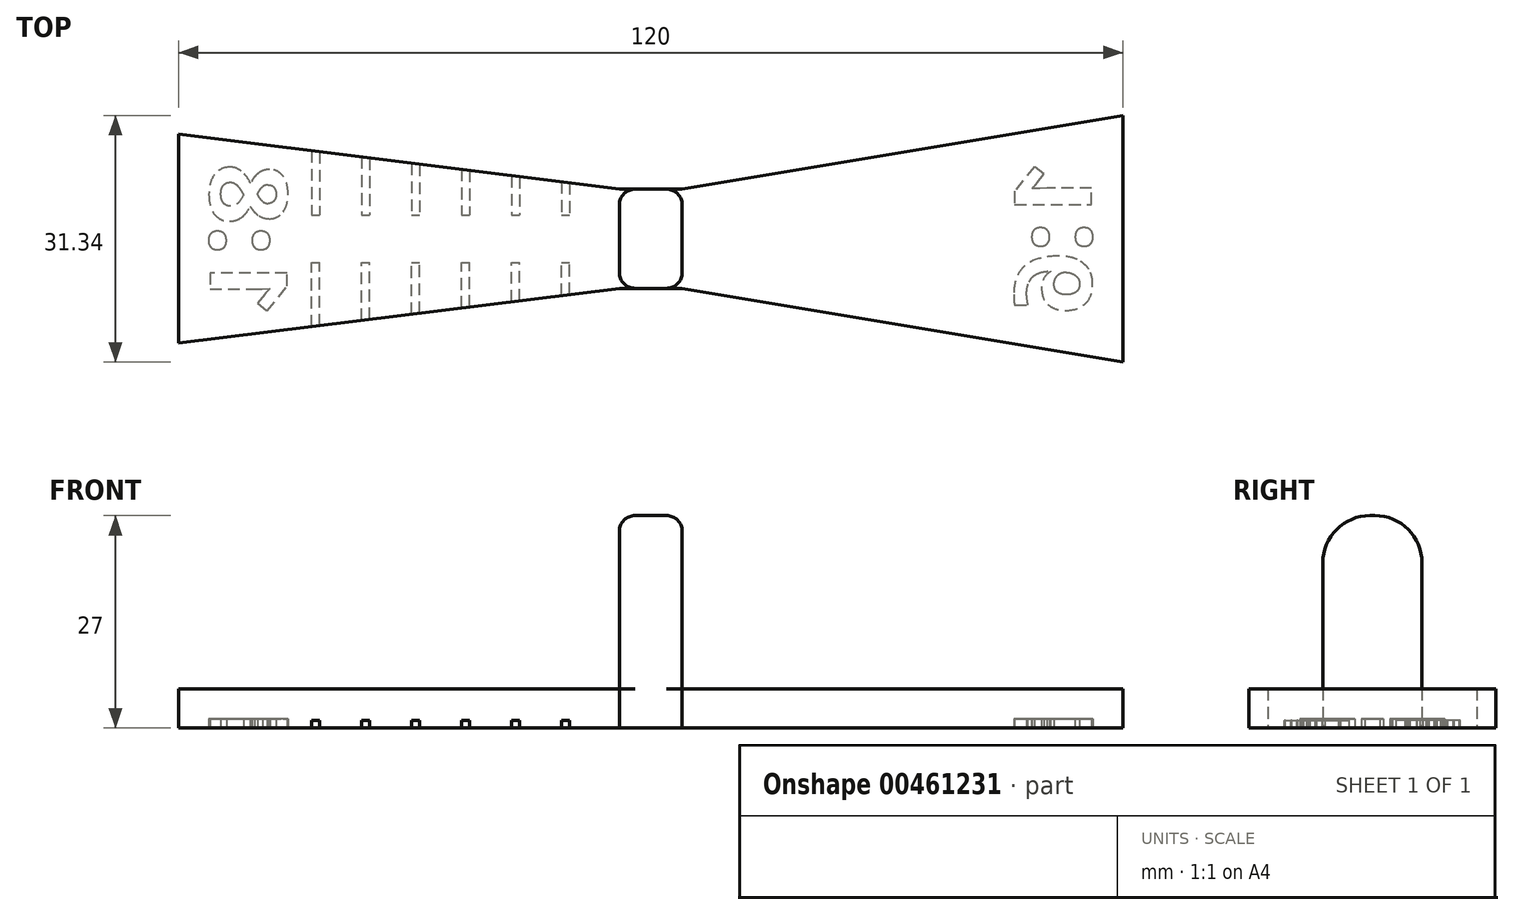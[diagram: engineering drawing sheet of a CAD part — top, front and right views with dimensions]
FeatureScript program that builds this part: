
annotation { "Feature Type Name" : "Feature", "Feature Type Description" : "" }
export const myFeature = defineFeature(function(context is Context, id is Id, definition is map)
    precondition{}
    {
        {
            var Q0;
            Q0=qCreatedBy(makeId("Top.planeOp"),FACE);
            var sketch = newSketch(context, id + "F0", { "sketchPlane" : qUnion([Q0])});
            skLineSegment(sketch, "E0", {"start": v(-4, 6.3) * mm, "end": v(-60, 13.28) * mm});
            skLineSegment(sketch, "E1", {"start": v(-60, 13.28) * mm, "end": v(-60, -13.28) * mm});
            skLineSegment(sketch, "E2", {"start": v(-60, -13.28) * mm, "end": v(-4, -6.3) * mm});
            skLineSegment(sketch, "E3", {"start": v(-4, -6.3) * mm, "end": v(4, -6.3) * mm});
            skLineSegment(sketch, "E4", {"start": v(4, -6.3) * mm, "end": v(60, -15.67) * mm});
            skLineSegment(sketch, "E5", {"start": v(60, -15.67) * mm, "end": v(60, 15.67) * mm});
            skLineSegment(sketch, "E6", {"start": v(60, 15.67) * mm, "end": v(4, 6.3) * mm});
            skLineSegment(sketch, "E7", {"start": v(4, 6.3) * mm, "end": v(-4, 6.3) * mm});
            skSolve(sketch);
        }
        {
            var Q0;
            Q0=makeQuery(id+"F0.imprint","IMPRINT",FACE,{"disambiguationData":[TD([[makeQuery(id+"F0.imprint","IMPRINT",EDGE,{"derivedFrom":sQuery(id+"F0.wireOp",EDGE,"E0")}),1.0]])]});
            extrude(context, id + "F1", {"entities" : qUnion([Q0]), "depth" : 5 * mm});
        }
        {
            var Q0;
            Q0=makeQuery(id+"F1.opExtrude","CAP_FACE",FACE,{"disambiguationData":[OSD([sQuery(id+"F0.wireOp",EDGE,"E0"),sQuery(id+"F0.wireOp",EDGE,"E1"),sQuery(id+"F0.wireOp",EDGE,"E2"),sQuery(id+"F0.wireOp",EDGE,"E3"),sQuery(id+"F0.wireOp",EDGE,"E4"),sQuery(id+"F0.wireOp",EDGE,"E5"),sQuery(id+"F0.wireOp",EDGE,"E6"),sQuery(id+"F0.wireOp",EDGE,"E7")])],"isStart":false});
            var sketch = newSketch(context, id + "F2", { "sketchPlane" : qUnion([Q0])});
            skLineSegment(sketch, "E8", {"start": v(-4, 6.3) * mm, "end": v(-4, -6.3) * mm});
            skLineSegment(sketch, "E9", {"start": v(-4, -6.3) * mm, "end": v(4, -6.3) * mm});
            skLineSegment(sketch, "E10", {"start": v(4, -6.3) * mm, "end": v(4, 6.3) * mm});
            skLineSegment(sketch, "E11", {"start": v(4, 6.3) * mm, "end": v(-4, 6.3) * mm});
            skSolve(sketch);
        }
        {
            var Q0;
            Q0 = qSketchRegion(id + "F2", true);
            extrude(context, id + "F3", {"entities" : qUnion([Q0]), "operationType" : NewBodyOperationType.ADD, "depth" : 22 * mm});
        }
        {
            var Q0;
            Q0=makeQuery(id+"F3.opExtrude","CAP_EDGE",EDGE,{"disambiguationData":[OSD([sQuery(id+"F2.wireOp",EDGE,"E9")])],"isStart":false});
            var Q1;
            Q1=makeQuery(id+"F3.opExtrude","CAP_EDGE",EDGE,{"disambiguationData":[OSD([sQuery(id+"F2.wireOp",EDGE,"E11")])],"isStart":false});
            fillet(context, id + "F4", {"entities" : qUnion([Q0, Q1]), "radius" : 6 * mm, "tangentPropagation" : true, "allowEdgeOverflow" : false});
        }
        {
            var Q0;
            Q0=makeQuery(id+"F3.opExtrude","CAP_EDGE",EDGE,{"disambiguationData":[OSD([sQuery(id+"F2.wireOp",EDGE,"E8")])],"isStart":false});
            var Q1;
            Q1=makeQuery(id+"F3.opExtrude","CAP_EDGE",EDGE,{"disambiguationData":[OSD([sQuery(id+"F2.wireOp",EDGE,"E10")])],"isStart":false});
            fillet(context, id + "F5", {"entities" : qUnion([Q0, Q1]), "radius" : 2 * mm, "tangentPropagation" : true, "allowEdgeOverflow" : false});
        }
        {
            var Q0;
            Q0=makeQuery(id+"F1.opExtrude","CAP_FACE",FACE,{"disambiguationData":[OSD([sQuery(id+"F0.wireOp",EDGE,"E0"),sQuery(id+"F0.wireOp",EDGE,"E1"),sQuery(id+"F0.wireOp",EDGE,"E2"),sQuery(id+"F0.wireOp",EDGE,"E3"),sQuery(id+"F0.wireOp",EDGE,"E4"),sQuery(id+"F0.wireOp",EDGE,"E5"),sQuery(id+"F0.wireOp",EDGE,"E6"),sQuery(id+"F0.wireOp",EDGE,"E7")])],"isStart":true});
            var sketch = newSketch(context, id + "F6", { "sketchPlane" : qUnion([Q0])});
            skText(sketch, "E12", { "text": "1:8", "fontName": "OpenSans-Bold.ttf"});
            skText(sketch, "E13", { "text": "1:6", "fontName": "OpenSans-Bold.ttf"});
            const initialGuessF6  = {"E12": [-0.056, 0.01, 0, -1, 0.00988], "E13": [0.056, -0.01, 0, 1, 0.00986]};
            skSetInitialGuess(sketch, initialGuessF6);
            skSolve(sketch);
        }
        {
            var Q0;
            Q0 = qSketchRegion(id + "F6", true);
            extrude(context, id + "F7", {"entities" : qUnion([Q0]), "operationType" : NewBodyOperationType.REMOVE, "oppositeDirection" : true, "depth" : 1.2 * mm});
        }
        {
            var Q0;
            {var subQ0=sQuery(id+"F0.wireOp",EDGE,"E7");var subQ1=sQuery(id+"F0.wireOp",EDGE,"E0");var subQ2=sQuery(id+"F0.wireOp",EDGE,"E6");var subQ3=sQuery(id+"F0.wireOp",EDGE,"E5");var subQ4=sQuery(id+"F0.wireOp",EDGE,"E4");var subQ5=sQuery(id+"F0.wireOp",EDGE,"E1");var subQ6=sQuery(id+"F0.wireOp",EDGE,"E2");var subQ7=sQuery(id+"F0.wireOp",EDGE,"E3");Q0=makeQuery(id+"F7.boolean.opBoolean","SPLIT",FACE,{"disambiguationData":[TD([makeQuery(id+"F1.opExtrude","SWEPT_FACE",FACE,{"disambiguationData":[OSD([subQ1])]})])],"derivedFrom":makeQuery(id+"F1.opExtrude","CAP_FACE",FACE,{"disambiguationData":[OSD([subQ1,subQ5,subQ6,subQ7,subQ4,subQ3,subQ2,subQ0])],"isStart":true})});}
            var sketch = newSketch(context, id + "F8", { "sketchPlane" : qUnion([Q0])});
            skLineSegment(sketch, "E14.bottom", {"start": v(-11.35, 13) * mm, "end": v(-10.35, 13) * mm});
            skLineSegment(sketch, "E14.top", {"start": v(-11.35, 3) * mm, "end": v(-10.35, 3) * mm});
            skLineSegment(sketch, "E14.left", {"start": v(-11.35, 13) * mm, "end": v(-11.35, 3) * mm});
            skLineSegment(sketch, "E14.right", {"start": v(-10.35, 13) * mm, "end": v(-10.35, 3) * mm});
            skLineSegment(sketch, "E15.1.0.0", {"start": v(-16.7, 13) * mm, "end": v(-16.7, 3) * mm});
            skLineSegment(sketch, "E15.1.0.1", {"start": v(-17.7, 13) * mm, "end": v(-16.7, 13) * mm});
            skLineSegment(sketch, "E15.1.0.2", {"start": v(-17.7, 13) * mm, "end": v(-17.7, 3) * mm});
            skLineSegment(sketch, "E15.1.0.3", {"start": v(-17.7, 3) * mm, "end": v(-16.7, 3) * mm});
            skLineSegment(sketch, "E15.2.0.0", {"start": v(-23.05, 13) * mm, "end": v(-23.05, 3) * mm});
            skLineSegment(sketch, "E15.2.0.1", {"start": v(-24.05, 13) * mm, "end": v(-23.05, 13) * mm});
            skLineSegment(sketch, "E15.2.0.2", {"start": v(-24.05, 13) * mm, "end": v(-24.05, 3) * mm});
            skLineSegment(sketch, "E15.2.0.3", {"start": v(-24.05, 3) * mm, "end": v(-23.05, 3) * mm});
            skLineSegment(sketch, "E15.3.0.0", {"start": v(-29.4, 13) * mm, "end": v(-29.4, 3) * mm});
            skLineSegment(sketch, "E15.3.0.1", {"start": v(-30.4, 13) * mm, "end": v(-29.4, 13) * mm});
            skLineSegment(sketch, "E15.3.0.2", {"start": v(-30.4, 13) * mm, "end": v(-30.4, 3) * mm});
            skLineSegment(sketch, "E15.3.0.3", {"start": v(-30.4, 3) * mm, "end": v(-29.4, 3) * mm});
            skLineSegment(sketch, "E15.4.0.0", {"start": v(-35.75, 13) * mm, "end": v(-35.75, 3) * mm});
            skLineSegment(sketch, "E15.4.0.1", {"start": v(-36.75, 13) * mm, "end": v(-35.75, 13) * mm});
            skLineSegment(sketch, "E15.4.0.2", {"start": v(-36.75, 13) * mm, "end": v(-36.75, 3) * mm});
            skLineSegment(sketch, "E15.4.0.3", {"start": v(-36.75, 3) * mm, "end": v(-35.75, 3) * mm});
            skLineSegment(sketch, "E15.direction1", {"start": v(-10.35, 3) * mm, "end": v(-16.7, 3) * mm, "construction": true});
            skLineSegment(sketch, "E16.0.5.0", {"start": v(-42.1, 13) * mm, "end": v(-42.1, 3) * mm});
            skLineSegment(sketch, "E16.3.5.0", {"start": v(-43.1, 13) * mm, "end": v(-42.1, 13) * mm});
            skLineSegment(sketch, "E16.6.5.0", {"start": v(-43.1, 13) * mm, "end": v(-43.1, 3) * mm});
            skLineSegment(sketch, "E16.9.5.0", {"start": v(-43.1, 3) * mm, "end": v(-42.1, 3) * mm});
            skLineSegment(sketch, "E17", {"start": v(-16.1, 0) * mm, "end": v(-40.75, 0) * mm, "construction": true});
            skLineSegment(sketch, "E18.MirrorCS", {"start": v(-30.4, -13) * mm, "end": v(-29.4, -13) * mm});
            skLineSegment(sketch, "E19.MirrorCS", {"start": v(-24.05, -13) * mm, "end": v(-23.05, -13) * mm});
            skLineSegment(sketch, "E20.MirrorCS", {"start": v(-30.4, -3) * mm, "end": v(-29.4, -3) * mm});
            skLineSegment(sketch, "E21.MirrorCS", {"start": v(-24.05, -3) * mm, "end": v(-23.05, -3) * mm});
            skLineSegment(sketch, "E22.MirrorCS", {"start": v(-43.1, -13) * mm, "end": v(-42.1, -13) * mm});
            skLineSegment(sketch, "E23.MirrorCS", {"start": v(-43.1, -3) * mm, "end": v(-42.1, -3) * mm});
            skLineSegment(sketch, "E24.MirrorCS", {"start": v(-36.75, -3) * mm, "end": v(-35.75, -3) * mm});
            skLineSegment(sketch, "E25.MirrorCS", {"start": v(-36.75, -13) * mm, "end": v(-35.75, -13) * mm});
            skLineSegment(sketch, "E26.MirrorCS", {"start": v(-36.75, -13) * mm, "end": v(-36.75, -3) * mm});
            skLineSegment(sketch, "E27.MirrorCS", {"start": v(-43.1, -13) * mm, "end": v(-43.1, -3) * mm});
            skLineSegment(sketch, "E28.MirrorCS", {"start": v(-30.4, -13) * mm, "end": v(-30.4, -3) * mm});
            skLineSegment(sketch, "E29.MirrorCS", {"start": v(-23.05, -13) * mm, "end": v(-23.05, -3) * mm});
            skLineSegment(sketch, "E30.MirrorCS", {"start": v(-42.1, -13) * mm, "end": v(-42.1, -3) * mm});
            skLineSegment(sketch, "E31.MirrorCS", {"start": v(-29.4, -13) * mm, "end": v(-29.4, -3) * mm});
            skLineSegment(sketch, "E32.MirrorCS", {"start": v(-24.05, -13) * mm, "end": v(-24.05, -3) * mm});
            skLineSegment(sketch, "E33.MirrorCS", {"start": v(-35.75, -13) * mm, "end": v(-35.75, -3) * mm});
            skLineSegment(sketch, "E34.MirrorCS", {"start": v(-17.7, -13) * mm, "end": v(-16.7, -13) * mm});
            skLineSegment(sketch, "E35.MirrorCS", {"start": v(-17.7, -13) * mm, "end": v(-17.7, -3) * mm});
            skLineSegment(sketch, "E36.MirrorCS", {"start": v(-16.7, -13) * mm, "end": v(-16.7, -3) * mm});
            skLineSegment(sketch, "E37.MirrorCS", {"start": v(-17.7, -3) * mm, "end": v(-16.7, -3) * mm});
            skLineSegment(sketch, "E38.MirrorCS", {"start": v(-11.35, -3) * mm, "end": v(-10.35, -3) * mm});
            skLineSegment(sketch, "E39.MirrorCS", {"start": v(-11.35, -13) * mm, "end": v(-11.35, -3) * mm});
            skLineSegment(sketch, "E40.MirrorCS", {"start": v(-10.35, -13) * mm, "end": v(-10.35, -3) * mm});
            skLineSegment(sketch, "E41.MirrorCS", {"start": v(-11.35, -13) * mm, "end": v(-10.35, -13) * mm});
            skSolve(sketch);
        }
        {
            var Q0;
            Q0 = qSketchRegion(id + "F8", true);
            extrude(context, id + "F9", {"entities" : qUnion([Q0]), "operationType" : NewBodyOperationType.REMOVE, "oppositeDirection" : true, "depth" : 1 * mm});
        }
    });
